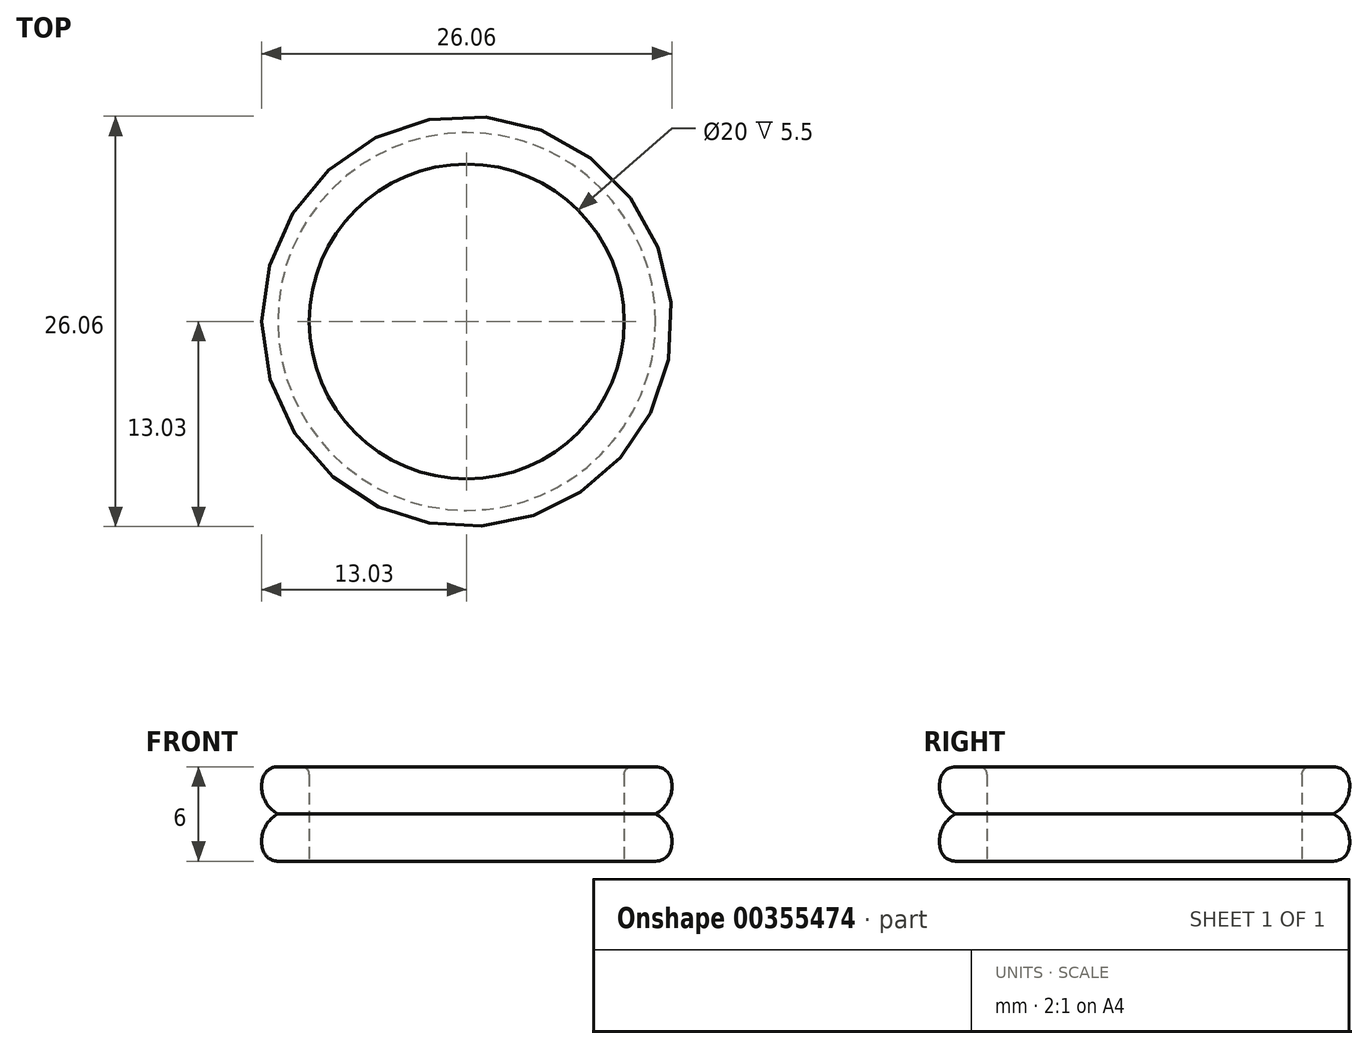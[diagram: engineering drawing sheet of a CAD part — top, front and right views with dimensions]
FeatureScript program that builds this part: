
annotation { "Feature Type Name" : "Feature", "Feature Type Description" : "" }
export const myFeature = defineFeature(function(context is Context, id is Id, definition is map)
    precondition{}
    {
        {
            var Q0;
            Q0=qCreatedBy(makeId("Front.planeOp"),FACE);
            var sketch = newSketch(context, id + "F0", { "sketchPlane" : qUnion([Q0])});
            skLineSegment(sketch, "E0", {"start": v(0, 0) * mm, "end": v(0, 5.5) * mm});
            skLineSegment(sketch, "E1", {"start": v(-0.5, 6) * mm, "end": v(-2, 6) * mm});
            skLineSegment(sketch, "E2", {"start": v(0, 0) * mm, "end": v(-2, 0) * mm});
            skPoint(sketch, "E3.visualSharp", {"position": v(-3, 6) * mm});
            skPoint(sketch, "E4.visualSharp", {"position": v(0, 0) * mm});
            skLineSegment(sketch, "E4.filletArc", {"start": v(0, 0) * mm, "end": v(0, 0) * mm});
            skLineSegment(sketch, "E5.0", {"start": v(10, 0) * mm, "end": v(10, 6) * mm});
            skLineSegment(sketch, "E6", {"start": v(0, 3) * mm, "end": v(-2, 3) * mm});
            skPoint(sketch, "E6.endSnap0", {"position": v(0, 3) * mm});
            skArc(sketch, "E7", {"start": v(-2.97, 5.25) * mm, "mid": v(-2.87, 3.96) * mm, "end": v(-2, 3) * mm});
            skArc(sketch, "E8", {"start": v(-2, 3) * mm, "mid": v(-2.87, 2.04) * mm, "end": v(-2.97, 0.75) * mm});
            skPoint(sketch, "E9.visualSharp", {"position": v(-2.6, 6) * mm});
            skArc(sketch, "E9.filletArc", {"start": v(-2.5, 6) * mm, "mid": v(-2.58, 5.98) * mm, "end": v(-2.65, 5.92) * mm});
            skArc(sketch, "E10.filletArc", {"start": v(-2, 6) * mm, "mid": v(-2.6, 5.8) * mm, "end": v(-2.97, 5.25) * mm});
            skPoint(sketch, "E11.visualSharp", {"position": v(-2.6, 0) * mm});
            skArc(sketch, "E11.filletArc", {"start": v(-2.97, 0.75) * mm, "mid": v(-2.6, 0.2) * mm, "end": v(-2, 0) * mm});
            skPoint(sketch, "E12.visualSharp", {"position": v(0, 6) * mm});
            skArc(sketch, "E12.filletArc", {"start": v(0, 5.5) * mm, "mid": v(-0.15, 5.85) * mm, "end": v(-0.5, 6) * mm});
            skSolve(sketch);
        }
        {
            var Q0;
            Q0 = qSketchRegion(id + "F0", true);
            var Q1;
            Q1=sQuery(id+"F0.wireOp",EDGE,"E5.0");
            revolve(context, id + "F1", {"entities" : qUnion([Q0]), "axis" : qUnion([Q1]), "revolveType" : RevolveType.FULL});
        }
    });
